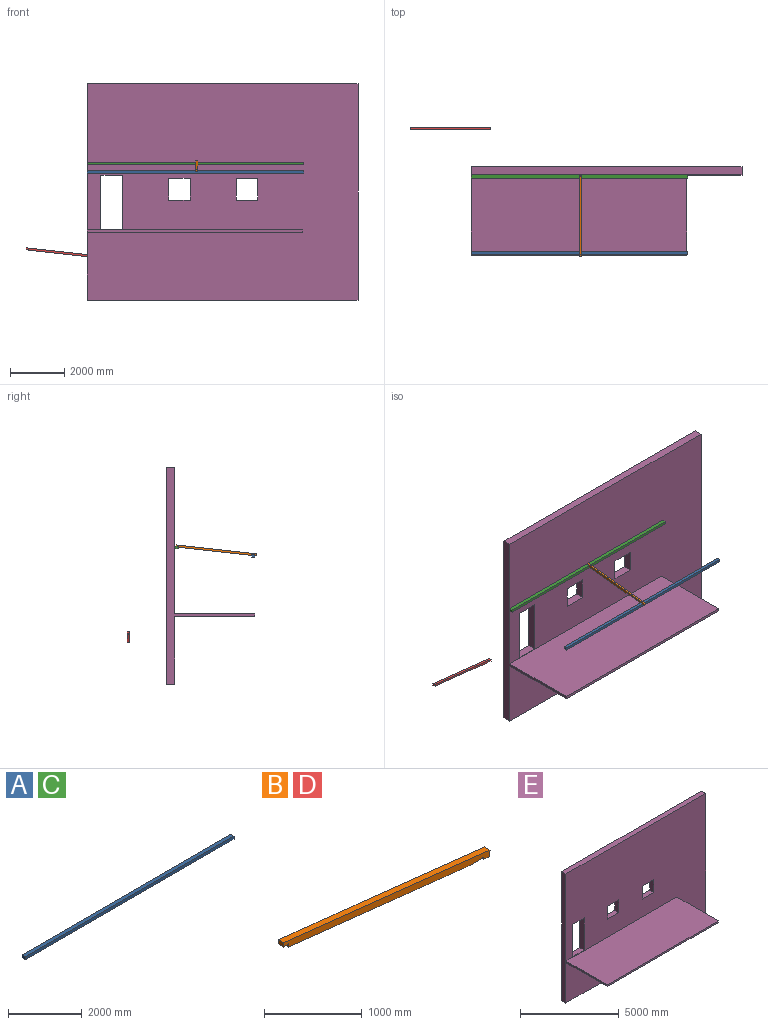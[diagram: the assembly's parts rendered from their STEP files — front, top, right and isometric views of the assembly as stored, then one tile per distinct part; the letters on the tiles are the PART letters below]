
ASSEMBLY  parts=5 mates=8
PART A: 6 faces, bbox 8000x120x100 mm
  f0: plane 8000x120mm, normal (0,0,1), area 960000mm2, adj f1,f3,f4,f5
  f1: plane 8000x100mm, normal (0,-1,0), area 800000mm2, adj f0,f2,f4,f5
  f2: plane 8000x120mm, normal (0,0,-1), area 960000mm2, adj f1,f3,f4,f5
  f3: plane 8000x100mm, normal (0,1,0), area 800000mm2, adj f0,f2,f4,f5
  f4: plane 120x100mm, normal (1,0,0), area 12000mm2, adj f0,f1,f2,f3
  f5: plane 120x100mm, normal (-1,0,0), area 12000mm2, adj f0,f1,f2,f3
PART B: 11 faces, bbox 2987.3x80x408.7 mm
  f0: plane 80x49.52mm, normal (-0.99,0,0.11), area 3985.4mm2, adj f3,f4,f5,f9
  f1: plane 2592.08x286.17mm, normal (-0.11,0,-0.99), area 208626mm2, adj f3,f4,f7,f10
  f2: plane 81.88x80mm, normal (-0.11,0,-0.99), area 6590.4mm2, adj f3,f4,f6,f8
  f3: plane 2987.35x408.72mm, normal (0,-1,0), area 234428.8mm2, adj f0,f1,f2,f5,f6,f7,f8,f9
  f4: plane 2987.35x408.72mm, normal (0,1,0), area 234428.8mm2, adj f0,f1,f2,f5,f6,f7,f8,f9
  f5: plane 2981.88x329.2mm, normal (0.11,0,0.99), area 240000mm2, adj f0,f3,f4,f6
  f6: plane 80x79.52mm, normal (0.99,0,-0.11), area 6400mm2, adj f2,f3,f4,f5
  f7: plane 227.92x80mm, normal (0,0,-1), area 18233.9mm2, adj f1,f3,f4,f8
  f8: plane 80x25.16mm, normal (-1,0,0), area 2013mm2, adj f2,f3,f4,f7
  f9: plane 80x76.69mm, normal (0,0,-1), area 6135mm2, adj f0,f3,f4,f10
  f10: plane 80x38.83mm, normal (-1,0,0), area 3106.6mm2, adj f1,f3,f4,f9
PART C: same geometry as A
PART D: same geometry as B
PART E: 22 faces, bbox 10000x3260x8000 mm
  f0: plane 10000x300mm, normal (0,0,1), area 3000000mm2, adj f1,f3,f4,f5
  f1: plane 8000x3260mm, normal (-1,0,0), area 2696000mm2, adj f0,f2,f4,f5,f18,f20,f21
  f2: plane 10000x300mm, normal (0,0,-1), area 3000000mm2, adj f1,f3,f4,f5
  f3: plane 8000x300mm, normal (1,0,0), area 2400000mm2, adj f0,f2,f4,f5
  f4: plane 10000x8000mm, normal (0,1,0), area 77120000mm2, adj f0,f1,f2,f3,f6,f7,f8,f9
  f5: plane 10000x8000mm, normal (0,-1,0), area 76325000mm2, adj f0,f1,f2,f3,f6,f7,f8,f9
  f6: plane 800x300mm, normal (0,0,-1), area 240000mm2, adj f4,f5,f7,f9
  f7: plane 800x300mm, normal (1,0,0), area 240000mm2, adj f4,f5,f6,f8
  f8: plane 800x300mm, normal (0,0,1), area 240000mm2, adj f4,f5,f7,f9
  f9: plane 800x300mm, normal (-1,0,0), area 240000mm2, adj f4,f5,f6,f8
  f10: plane 800x300mm, normal (0,0,-1), area 240000mm2, adj f4,f5,f11,f13
  f11: plane 800x300mm, normal (1,0,0), area 240000mm2, adj f4,f5,f10,f12
  f12: plane 800x300mm, normal (0,0,1), area 240000mm2, adj f4,f5,f11,f13
  f13: plane 800x300mm, normal (-1,0,0), area 240000mm2, adj f4,f5,f10,f12
  f14: plane 800x300mm, normal (0,0,-1), area 240000mm2, adj f4,f5,f15,f17
  f15: plane 2000x300mm, normal (1,0,0), area 600000mm2, adj f4,f5,f14,f16
  f16: plane 800x300mm, normal (0,0,1), area 240000mm2, adj f4,f5,f15,f17
  f17: plane 2000x300mm, normal (-1,0,0), area 600000mm2, adj f4,f5,f14,f16
  f18: plane 7950x100mm, normal (0,-1,0), area 795000mm2, adj f1,f19,f20,f21
  f19: plane 2960x100mm, normal (1,0,0), area 296000mm2, adj f5,f18,f20,f21
  f20: plane 7950x2960mm, normal (0,0,1), area 23532000mm2, adj f1,f5,f18,f19
  f21: plane 7950x2960mm, normal (0,0,-1), area 23532000mm2, adj f1,f5,f18,f19
PLACE A t=(0,-2900,2250)mm
PLACE B rot(axis=(0,0,-1),90deg) t=(4038.34,-40,2510)mm
PLACE C t=(0,-60,2550)mm
PLACE D t=(-2271.08,1726.09,-701.97)mm
PLACE E at identity fixed
MATE planar C.f3 <-> E.f5  axis (0,1,0) through (4000,0,2550)mm
MATE planar B.f9 <-> C.f0  axis (0,0,-1) through (4038.34,-81.66,2600)mm
MATE planar B.f10 <-> C.f1  axis (0,1,0) through (4038.34,-120,2580.58)mm
MATE parallel C.f2 <-> E.f20  axis (0,0,-1) through (4000,-60,2500)mm
MATE planar A.f5 <-> E.f1  axis (-1,0,0) through (0,-2900,2250)mm
MATE planar A.f1 <-> E.f18  axis (0,-1,0) through (4000,-2960,2250)mm
MATE planar C.f5 <-> E.f1  axis (-1,0,0) through (0,-60,2550)mm
MATE parallel A.f2 <-> E.f20  axis (0,0,-1) through (4000,-2900,2200)mm
